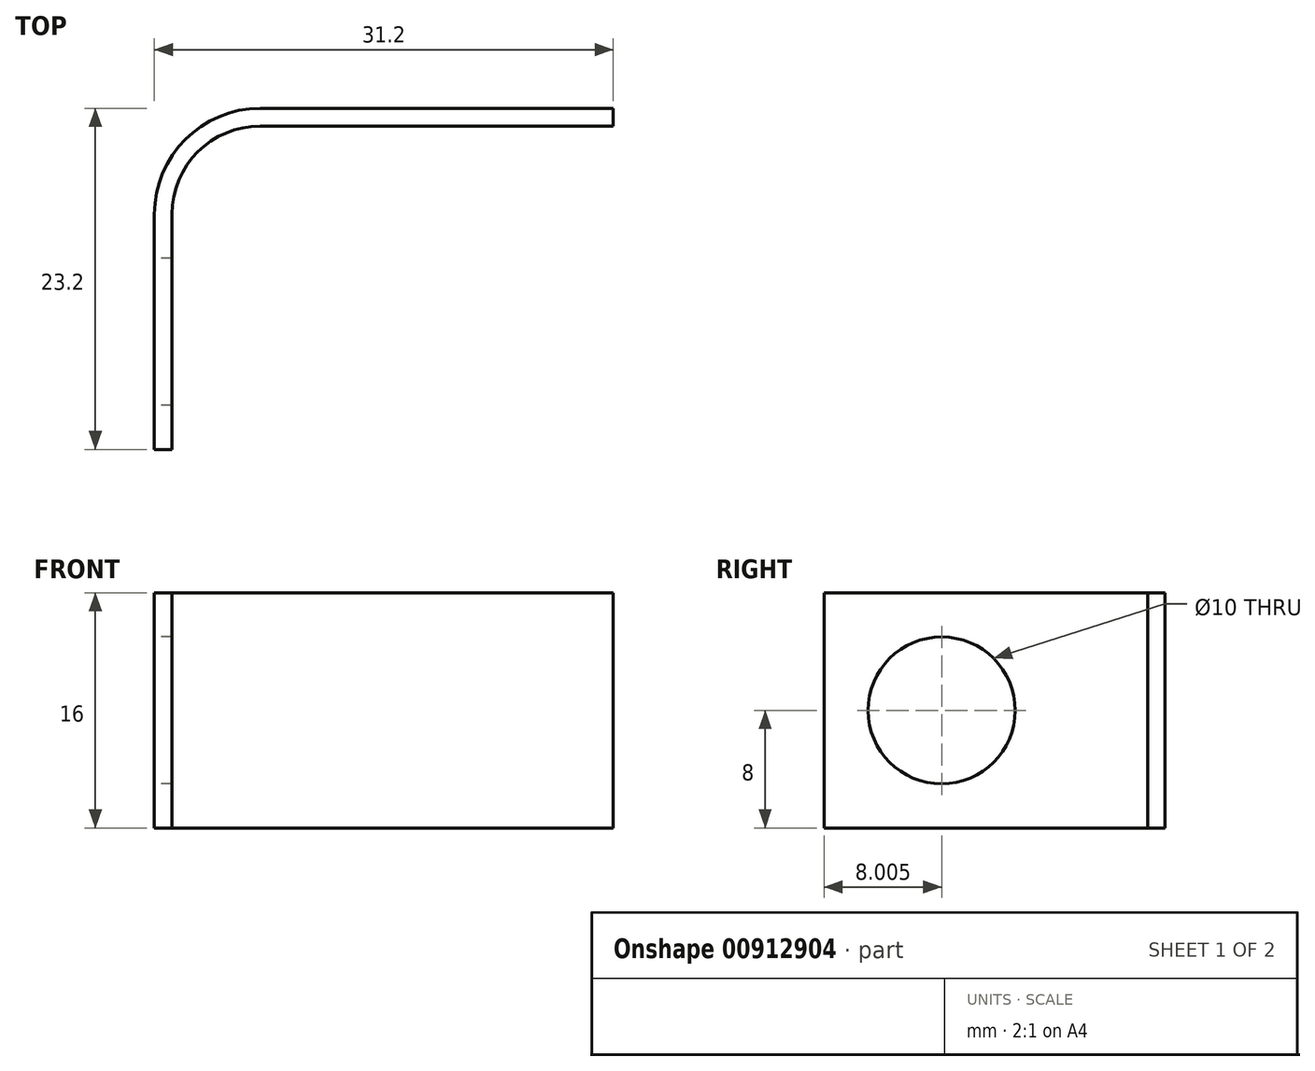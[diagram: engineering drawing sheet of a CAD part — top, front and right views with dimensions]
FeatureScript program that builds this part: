
annotation { "Feature Type Name" : "Feature", "Feature Type Description" : "" }
export const myFeature = defineFeature(function(context is Context, id is Id, definition is map)
    precondition{}
    {
        {
            var Q0;
            Q0=qCreatedBy(makeId("Top.planeOp"),FACE);
            var sketch = newSketch(context, id + "F0", { "sketchPlane" : qUnion([Q0])});
            skLineSegment(sketch, "E0", {"start": v(-48.19, 20.82) * mm, "end": v(-48.19, 36.82) * mm});
            skLineSegment(sketch, "E1", {"start": v(-42.19, 42.82) * mm, "end": v(-18.19, 42.82) * mm});
            skPoint(sketch, "E2.visualSharp", {"position": v(-48.19, 42.82) * mm});
            skArc(sketch, "E2.filletArc", {"start": v(-42.19, 42.82) * mm, "mid": v(-46.43, 41.07) * mm, "end": v(-48.19, 36.82) * mm});
            skLineSegment(sketch, "E3.0", {"start": v(-42.19, 44.02) * mm, "end": v(-18.19, 44.02) * mm});
            skArc(sketch, "E3.1", {"start": v(-42.19, 44.02) * mm, "mid": v(-47.28, 41.92) * mm, "end": v(-49.39, 36.82) * mm});
            skLineSegment(sketch, "E3.2", {"start": v(-49.39, 20.82) * mm, "end": v(-49.39, 36.82) * mm});
            skLineSegment(sketch, "E4", {"start": v(-48.19, 20.82) * mm, "end": v(-49.39, 20.82) * mm});
            skLineSegment(sketch, "E5", {"start": v(-18.19, 44.02) * mm, "end": v(-18.19, 42.82) * mm});
            skSolve(sketch);
        }
        {
            var Q0;
            Q0=makeQuery(id+"F0.imprint","IMPRINT",FACE,{"disambiguationData":[TD([[makeQuery(id+"F0.imprint","IMPRINT",EDGE,{"derivedFrom":sQuery(id+"F0.wireOp",EDGE,"E0")}),1.0]])]});
            extrude(context, id + "F1", {"entities" : qUnion([Q0]), "depth" : 16 * mm, "offsetDistance" : 25 * mm});
        }
        {
            var Q0;
            Q0=makeQuery(id+"F1.opExtrude","SWEPT_FACE",FACE,{"disambiguationData":[OSD([sQuery(id+"F0.wireOp",EDGE,"E3.2")])]});
            var sketch = newSketch(context, id + "F2", { "sketchPlane" : qUnion([Q0])});
            skLineSegment(sketch, "E6", {"start": v(-41.22, 8) * mm, "end": v(-19.02, 8) * mm, "construction": true});
            skPoint(sketch, "E6.startSnap0", {"position": v(-36.82, 8) * mm});
            skCircle(sketch, "E7", {"center": v(-28.82, 8) * mm, "radius": 5 * mm});
            skSolve(sketch);
        }
        {
            var Q0;
            Q0=makeQuery(id+"F2.imprint","IMPRINT",FACE,{"disambiguationData":[TD([[makeQuery(id+"F2.imprint","IMPRINT",EDGE,{"derivedFrom":sQuery(id+"F2.wireOp",EDGE,"E7")}),1.0]])]});
            extrude(context, id + "F3", {"entities" : qUnion([Q0]), "operationType" : NewBodyOperationType.REMOVE, "endBound" : BoundingType.THROUGH_ALL, "oppositeDirection" : true, "depth" : 25 * mm, "offsetDistance" : 25 * mm});
        }
    });
